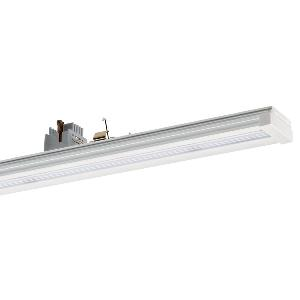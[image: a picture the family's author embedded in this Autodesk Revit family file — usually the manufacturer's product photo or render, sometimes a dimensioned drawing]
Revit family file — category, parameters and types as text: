
# Revit family: conveo_-_cvg_8000_840_xn-p_ea_5_226848219-00804959_f453
name_source: partatom
category: Lighting Fixtures
units: mm (PartAtom-declared; Revit-internal decimal feet)

## family parameters
Cut with Voids When Loaded = No
Host = Face
Light Source = No
Part Type = Normal
Room Calculation Point = No
Round Connector Dimension = Use Diameter
Shared = No

## types (1)
- CONVEO - CVG 8000/840/xN-P/EA/5 (1 x LED, 7600 lm, 4000K)
    Apparent Load = 55 VA
    Approval mark = CE
    CIE Flux Codes = 57 84 97 100 100
    Color Rendering = 80-89
    Color Temperature = 4000K
    Control Gear = Electronic ballast
    Default Elevation = 1800 mm
    Description = CVG 8000/840/xN-P/EA/5|Continuous-row system|light source: LED|work equipment: Electronic ballast|connected load: 220-240 V, 50-60 Hz|Power consumption: approx. 55 W|luminous flux: 7600 lm|luminous efficacy: 138 lm/W|colour temperature: Cold white, ca. 4000 K|color rendering index (CRI): >= 80|chromaticity tolerance:  3 SDCM|System of protection: IP 54|class of protection: I|technology: Switchable|luminaire body|material: Aluminium|surface: Powder coatet|colour: White|lamp cover: Acrylic (PMMA), Satine|weight (net): approx. 1.9 kg|Fastening: Available separately|minimum ambient temperature: -25 ░C|maximum ambient temperature: 47 ░C|glare control: Prism optics (linear)|Approval mark: VDE - ENEC|
    Frequency = 50 Hz
    Height = 70 mm
    Lamp = 1 x LED
    Lamp Light Flux = 7600 lm
    Lamp count = 1
    Length = 1500 mm
    Luminous efficacy = 138 lm/W
    Manufacturer = Waldmann
    ModVariant = No
    Model = 226848219-00804959
    Mounting Place = Ceiling
    Mounting Type = Pendant
    Number of Poles = 1
    OnlyDefault = Yes
    Power Factor = 1
    Product Name = CONVEO - CVG 8000/840/xN-P/EA/5
    Product group = Continuous-row system (industry)
    ProductGroupID = 301
    Protection Class = Protection class I
    Protection Degree = IP 54
    RLX_Detail_Level = 1
    RlxData = <blob elided: 99901 chars, md5=1ea71ea9>
    Socket = socket
    Standby Power = 0 W
    System Light Flux = 7600 lm
    System Power = 55 W
    Type Comments = Product without accessories
    Type Image = 226848079-00804943-1p5.jpg
    URL = http://relux.com
    VarID = ---
    Voltage = 230 V
    Voltage Range = 220-240 V
    Weight = 0.00 kg
    Width = 64 mm

## geometry (parser evidence)
native form markers: Blend x4, Sweep x7
no freeform markers — native parametric forms only
